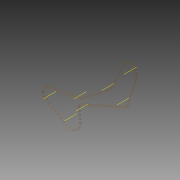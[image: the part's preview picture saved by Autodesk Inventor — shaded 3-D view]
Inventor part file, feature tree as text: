
AUTODESK INVENTOR PART (.ipt)
format: ipt  version: 2014 SP1 (Build 180222100, 222)  size: 430,592 bytes
history: native  units: mm (DEFAULTED — no unit token found)
features: other x96, extrude x86, sketch x2, plane x1, pattern_linear x1
ambient origin geometry x8: Origin, YZ Plane, XZ Plane, XY Plane, X Axis, Y Axis, Z Axis, Center Point
bodies: Body1 (feature_tree), Body2 (feature_tree), Body3 (feature_tree), Body4 (feature_tree), Body5 (feature_tree), Body6 (feature_tree), Body7 (feature_tree), Body8 (feature_tree), Body9 (feature_tree), Body10 (feature_tree), Body11 (feature_tree), Body12 (feature_tree), Body13 (feature_tree), Body14 (feature_tree), Body15 (feature_tree), Body16 (feature_tree), Body17 (feature_tree), Body18 (feature_tree), Body19 (feature_tree), Body20 (feature_tree), Body21 (feature_tree), Body22 (feature_tree), Body23 (feature_tree), Body24 (feature_tree), Body25 (feature_tree), Body26 (feature_tree), Body27 (feature_tree), Body28 (feature_tree), Body29 (feature_tree), Body30 (feature_tree), Body31 (feature_tree), Body32 (feature_tree), Body33 (feature_tree), Body34 (feature_tree), Body35 (feature_tree), Body36 (feature_tree), Body37 (feature_tree), Body38 (feature_tree), Body39 (feature_tree), Body40 (feature_tree), Body41 (feature_tree), Body42 (feature_tree), Body43 (feature_tree), Body44 (feature_tree), Body45 (feature_tree), Body46 (feature_tree), Body47 (feature_tree), Body48 (feature_tree), Body49 (feature_tree), Body50 (feature_tree), Body51 (feature_tree), Body52 (feature_tree), Body53 (feature_tree), Body54 (feature_tree), Body55 (feature_tree), Body56 (feature_tree), Body57 (feature_tree), Body58 (feature_tree), Body59 (feature_tree), Body60 (feature_tree), Body61 (feature_tree), Body62 (feature_tree), Body63 (feature_tree), Body64 (feature_tree), Body65 (feature_tree), Body66 (feature_tree), Body67 (feature_tree), Body68 (feature_tree), Body69 (feature_tree), Body70 (feature_tree), Body71 (feature_tree), Body72 (feature_tree), Body73 (feature_tree), Body74 (feature_tree), Body75 (feature_tree), Body76 (feature_tree), Body77 (feature_tree), Body78 (feature_tree), Body79 (feature_tree), Body80 (feature_tree), Body81 (feature_tree), Body82 (feature_tree), Body83 (feature_tree), Body84 (feature_tree), Body85 (feature_tree), Body86 (feature_tree)
feature tree (186):
  sketch  "Sketch Path"  dims[d1=10.6172mm d2=7.9375mm d3=2.682204mm d5=6.981317mm d7=0.0mm d8=0.0mm d9=0.0mm d10=0.0mm d11=0.0mm d12=0.0mm d13=0.0mm d14=0.0mm d15=2.54mm d16=0.0mm d17=2.54mm d18=0.0mm d19=850.0mm]
  other  "Cross Section Plane"
  other  "Work Axis1"
  other  "Work Axis2"
  other  "Work Axis3"
  other  "Work Axis4"
  other  "Work Axis5"
  other  "Work Axis6"
  other  "Work Axis7"
  other  "Work Point1"
  plane  "Work Plane2"
  pattern_linear  "Rectangular Pattern1"  Spacing1=7.9375mm  [1 undecoded]
  other  "Cross Section"
  other  "Srf1"
  sketch  "Sketch3"  dims[d0=0.0mm]
  other  "Srf2"
  other  "Srf3"
  other  "Srf4"
  other  "Srf5"
  other  "Srf6"
  other  "Srf7"
  other  "Srf8"
  other  "Srf9"
  other  "Srf10"
  other  "Srf11"
  other  "Srf12"
  other  "Srf13"
  other  "Srf14"
  other  "Srf15"
  other  "Srf16"
  other  "Srf17"
  other  "Srf18"
  other  "Srf19"
  other  "Srf20"
  other  "Srf21"
  other  "Srf22"
  other  "Srf23"
  other  "Srf24"
  other  "Srf25"
  other  "Srf26"
  other  "Srf27"
  other  "Srf28"
  other  "Srf29"
  other  "Srf30"
  other  "Srf31"
  other  "Srf32"
  other  "Srf33"
  other  "Srf34"
  other  "Srf35"
  other  "Srf36"
  other  "Srf37"
  other  "Srf38"
  other  "Srf39"
  other  "Srf40"
  other  "Srf41"
  other  "Srf42"
  other  "Srf43"
  other  "Srf44"
  other  "Srf45"
  other  "Srf46"
  other  "Srf47"
  other  "Srf48"
  other  "Srf49"
  other  "Srf50"
  other  "Srf51"
  other  "Srf52"
  other  "Srf53"
  other  "Srf54"
  other  "Srf55"
  other  "Srf56"
  other  "Srf57"
  other  "Srf58"
  other  "Srf59"
  other  "Srf60"
  other  "Srf61"
  other  "Srf62"
  other  "Srf63"
  other  "Srf64"
  other  "Srf65"
  other  "Srf66"
  other  "Srf67"
  other  "Srf68"
  other  "Srf69"
  other  "Srf70"
  other  "Srf71"
  other  "Srf72"
  other  "Srf73"
  other  "Srf74"
  other  "Srf75"
  other  "Srf76"
  other  "Srf77"
  other  "Srf78"
  other  "Srf79"
  other  "Srf80"
  other  "Srf81"
  other  "Srf82"
  other  "Srf83"
  other  "Srf84"
  other  "Srf85"
  other  "Srf86"
  extrude  "ExtrusionSrf1"  Depth=7.9375mm
  extrude  "ExtrusionSrf2"  Depth=7.9375mm
  extrude  "ExtrusionSrf3"  Depth=7.9375mm TaperAngle=0.0deg
  extrude  "ExtrusionSrf4"  Depth=7.9375mm TaperAngle=0.0deg
  extrude  "ExtrusionSrf5"  Depth=7.9375mm
  extrude  "ExtrusionSrf6"  [1 undecoded]
  extrude  "ExtrusionSrf7"  [1 undecoded]
  extrude  "ExtrusionSrf8"  [1 undecoded]
  extrude  "ExtrusionSrf9"  [1 undecoded]
  extrude  "ExtrusionSrf10"  [1 undecoded]
  extrude  "ExtrusionSrf11"  [1 undecoded]
  extrude  "ExtrusionSrf12"  [1 undecoded]
  extrude  "ExtrusionSrf13"  [1 undecoded]
  extrude  "ExtrusionSrf14"  [1 undecoded]
  extrude  "ExtrusionSrf15"  [1 undecoded]
  extrude  "ExtrusionSrf16"  [1 undecoded]
  extrude  "ExtrusionSrf17"  [1 undecoded]
  extrude  "ExtrusionSrf18"  [1 undecoded]
  extrude  "ExtrusionSrf19"  [1 undecoded]
  extrude  "ExtrusionSrf20"  [1 undecoded]
  extrude  "ExtrusionSrf21"  [1 undecoded]
  extrude  "ExtrusionSrf22"  [1 undecoded]
  extrude  "ExtrusionSrf23"  [1 undecoded]
  extrude  "ExtrusionSrf24"  [1 undecoded]
  extrude  "ExtrusionSrf25"  [1 undecoded]
  extrude  "ExtrusionSrf26"  [1 undecoded]
  extrude  "ExtrusionSrf27"  [1 undecoded]
  extrude  "ExtrusionSrf28"  [1 undecoded]
  extrude  "ExtrusionSrf29"  [1 undecoded]
  extrude  "ExtrusionSrf30"  [1 undecoded]
  extrude  "ExtrusionSrf31"  [1 undecoded]
  extrude  "ExtrusionSrf32"  [1 undecoded]
  extrude  "ExtrusionSrf33"  [1 undecoded]
  extrude  "ExtrusionSrf34"  [1 undecoded]
  extrude  "ExtrusionSrf35"  [1 undecoded]
  extrude  "ExtrusionSrf36"  [1 undecoded]
  extrude  "ExtrusionSrf37"  [1 undecoded]
  extrude  "ExtrusionSrf38"  [1 undecoded]
  extrude  "ExtrusionSrf39"  [1 undecoded]
  extrude  "ExtrusionSrf40"  [1 undecoded]
  extrude  "ExtrusionSrf41"  [1 undecoded]
  extrude  "ExtrusionSrf42"  [1 undecoded]
  extrude  "ExtrusionSrf43"  [1 undecoded]
  extrude  "ExtrusionSrf44"  [1 undecoded]
  extrude  "ExtrusionSrf45"  [1 undecoded]
  extrude  "ExtrusionSrf46"  [1 undecoded]
  extrude  "ExtrusionSrf47"  [1 undecoded]
  extrude  "ExtrusionSrf48"  [1 undecoded]
  extrude  "ExtrusionSrf49"  [1 undecoded]
  extrude  "ExtrusionSrf50"  [1 undecoded]
  extrude  "ExtrusionSrf51"  [1 undecoded]
  extrude  "ExtrusionSrf52"  [1 undecoded]
  extrude  "ExtrusionSrf53"  [1 undecoded]
  extrude  "ExtrusionSrf54"  [1 undecoded]
  extrude  "ExtrusionSrf55"  [1 undecoded]
  extrude  "ExtrusionSrf56"  [1 undecoded]
  extrude  "ExtrusionSrf57"  [1 undecoded]
  extrude  "ExtrusionSrf58"  [1 undecoded]
  extrude  "ExtrusionSrf59"  [1 undecoded]
  extrude  "ExtrusionSrf60"  [1 undecoded]
  extrude  "ExtrusionSrf61"  [1 undecoded]
  extrude  "ExtrusionSrf62"  [1 undecoded]
  extrude  "ExtrusionSrf63"  [1 undecoded]
  extrude  "ExtrusionSrf64"  [1 undecoded]
  extrude  "ExtrusionSrf65"  [1 undecoded]
  extrude  "ExtrusionSrf66"  [1 undecoded]
  extrude  "ExtrusionSrf67"  [1 undecoded]
  extrude  "ExtrusionSrf68"  [1 undecoded]
  extrude  "ExtrusionSrf69"  [1 undecoded]
  extrude  "ExtrusionSrf70"  [1 undecoded]
  extrude  "ExtrusionSrf71"  [1 undecoded]
  extrude  "ExtrusionSrf72"  [1 undecoded]
  extrude  "ExtrusionSrf73"  [1 undecoded]
  extrude  "ExtrusionSrf74"  [1 undecoded]
  extrude  "ExtrusionSrf75"  [1 undecoded]
  extrude  "ExtrusionSrf76"  [1 undecoded]
  extrude  "ExtrusionSrf77"  [1 undecoded]
  extrude  "ExtrusionSrf78"  [1 undecoded]
  extrude  "ExtrusionSrf79"  [1 undecoded]
  extrude  "ExtrusionSrf80"  [1 undecoded]
  extrude  "ExtrusionSrf81"  [1 undecoded]
  extrude  "ExtrusionSrf82"  [1 undecoded]
  extrude  "ExtrusionSrf83"  [1 undecoded]
  extrude  "ExtrusionSrf84"  [1 undecoded]
  extrude  "ExtrusionSrf85"  [1 undecoded]
  extrude  "ExtrusionSrf86"  [1 undecoded]
note: 82 required parameter values undecoded (feature->parameter linkage not recoverable at this tier; creation-order binding heuristic only, values carry confidence <= 0.55)
